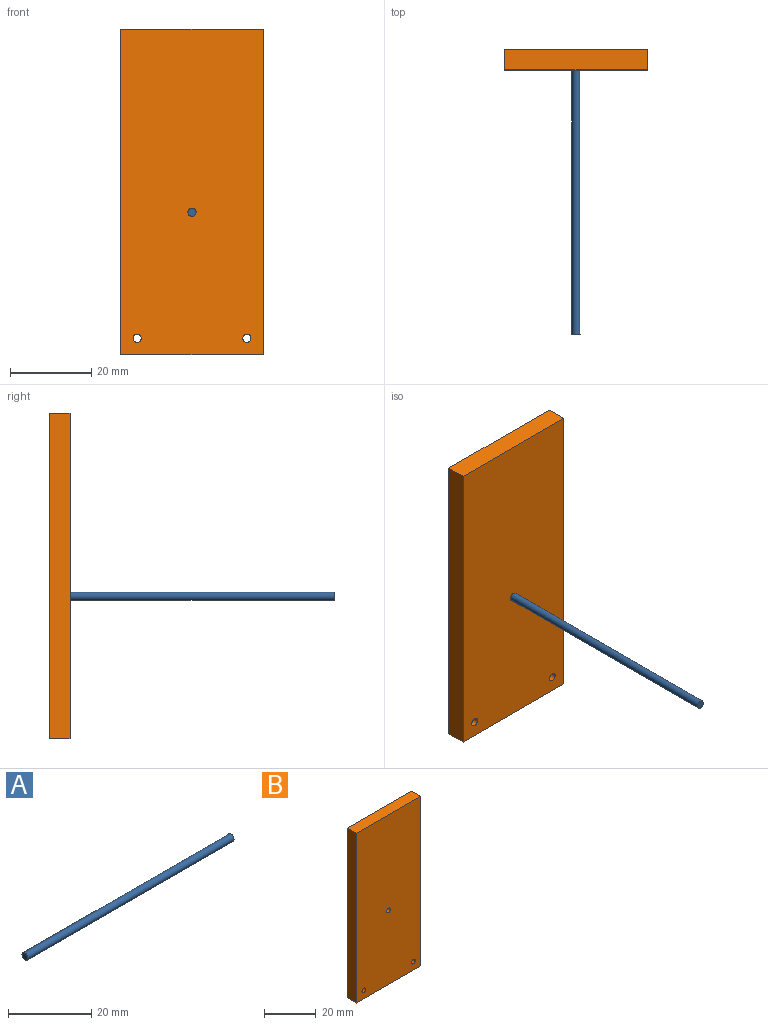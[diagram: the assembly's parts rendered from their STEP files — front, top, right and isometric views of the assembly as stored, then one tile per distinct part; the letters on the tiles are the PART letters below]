
ASSEMBLY  parts=2 mates=1
PART A: 3 faces, bbox 70x2x2 mm
  f0: cylinder r=1mm len=70mm, axis (-1,0,0), area 439.8mm2, adj f1,f2
  f1: plane 2x2mm, normal (-1,0,0), area 3.1mm2, adj f0
  f2: plane 2x2mm, normal (1,0,0), area 3.1mm2, adj f0
PART B: 9 faces, bbox 35x5x80 mm
  f0: plane 80x5mm, normal (-1,0,0), area 400mm2, adj f1,f5,f7,f8
  f1: plane 35x5mm, normal (0,0,-1), area 175mm2, adj f0,f2,f7,f8
  f2: plane 80x5mm, normal (1,0,0), area 400mm2, adj f1,f5,f7,f8
  f3: cylinder r=1mm len=5mm, axis (0,1,0), area 31.4mm2, adj f7,f8
  f4: cylinder r=1mm len=5mm, axis (0,1,0), area 31.4mm2, adj f7,f8
  f5: plane 35x5mm, normal (0,0,1), area 175mm2, adj f0,f2,f7,f8
  f6: cylinder r=1mm len=5mm, axis (0,1,0), area 31.4mm2, adj f7,f8
  f7: plane 80x35mm, normal (0,-1,0), area 2790.6mm2, adj f0,f1,f2,f3,f4,f5,f6
  f8: plane 80x35mm, normal (0,1,0), area 2790.6mm2, adj f0,f1,f2,f3,f4,f5,f6
PLACE A rot(axis=(0.58,-0.58,-0.58),120deg) t=(-63.03,-1.36,3.62)mm
PLACE B t=(-55.65,-10.51,0.34)mm
MATE cylindrical A.f0 <-> B.f6  axis (0,1,0) through (-63.03,-10.51,18.33)mm
